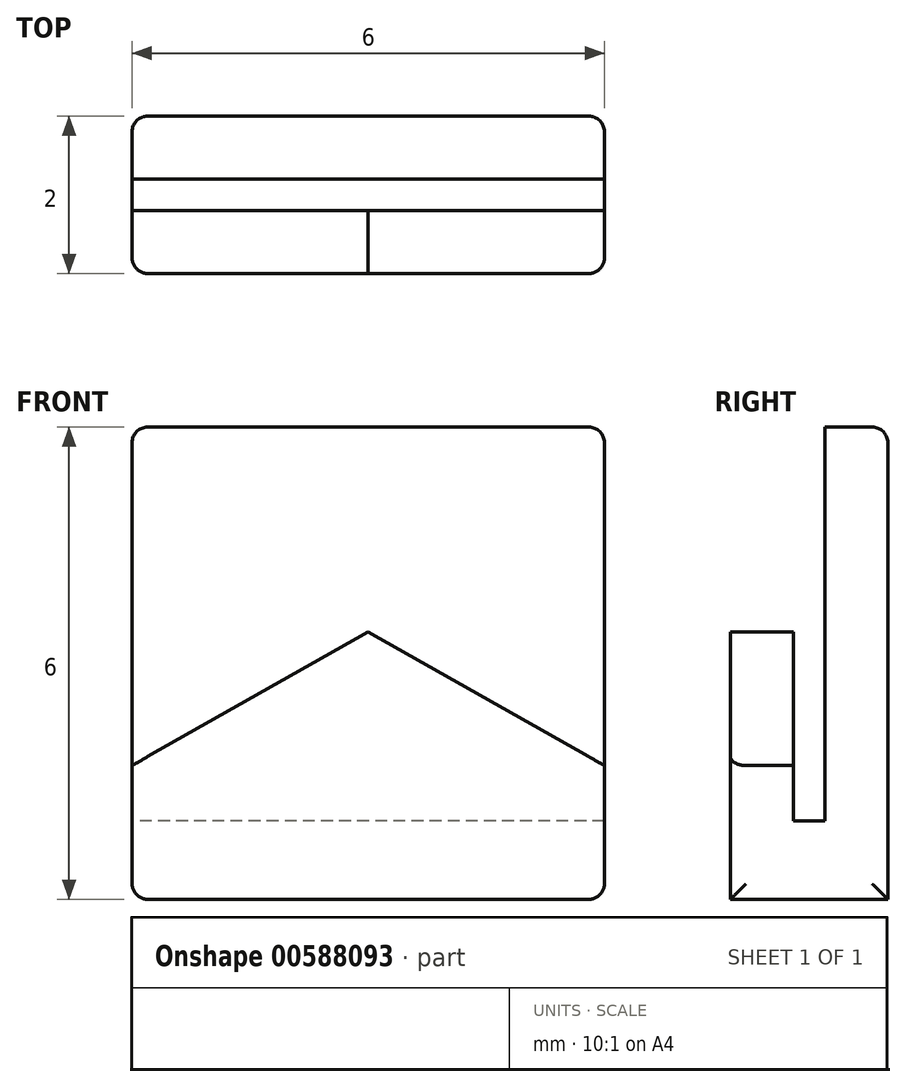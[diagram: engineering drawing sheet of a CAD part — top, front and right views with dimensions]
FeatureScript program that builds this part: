
annotation { "Feature Type Name" : "Feature", "Feature Type Description" : "" }
export const myFeature = defineFeature(function(context is Context, id is Id, definition is map)
    precondition{}
    {
        {
            var Q0;
            Q0=qCreatedBy(makeId("Top.planeOp"),FACE);
            var sketch = newSketch(context, id + "F0", { "sketchPlane" : qUnion([Q0])});
            skLineSegment(sketch, "E0.bottom", {"start": v(3, -1) * mm, "end": v(-3, -1) * mm});
            skLineSegment(sketch, "E0.top", {"start": v(3, 1) * mm, "end": v(-3, 1) * mm});
            skLineSegment(sketch, "E0.left", {"start": v(3, -1) * mm, "end": v(3, 1) * mm});
            skLineSegment(sketch, "E0.right", {"start": v(-3, -1) * mm, "end": v(-3, 1) * mm});
            skPoint(sketch, "E0.middle", {"position": v(0, 0) * mm});
            skLineSegment(sketch, "E1.bottom", {"start": v(3, 0.2) * mm, "end": v(-3, 0.2) * mm});
            skLineSegment(sketch, "E1.top", {"start": v(3, -0.2) * mm, "end": v(-3, -0.2) * mm});
            skLineSegment(sketch, "E1.left", {"start": v(3, 0.2) * mm, "end": v(3, -0.2) * mm});
            skLineSegment(sketch, "E1.right", {"start": v(-3, 0.2) * mm, "end": v(-3, -0.2) * mm});
            skSolve(sketch);
        }
        {
            var Q0;
            {var subQ0=sQuery(id+"F0.wireOp",EDGE,"E0.bottom");Q0=makeQuery(id+"F0.imprint","IMPRINT",FACE,{"disambiguationData":[TD([[makeQuery(id+"F0.imprint","IMPRINT",EDGE,{"derivedFrom":subQ0}),-1.0]])]});}
            var Q1;
            Q1=makeQuery(id+"F0.imprint","IMPRINT",FACE,{"disambiguationData":[TD([[makeQuery(id+"F0.imprint","IMPRINT",EDGE,{"derivedFrom":sQuery(id+"F0.wireOp",EDGE,"E1.bottom")}),1.0]])]});
            var Q2;
            {var subQ0=sQuery(id+"F0.wireOp",EDGE,"E0.top");Q2=makeQuery(id+"F0.imprint","IMPRINT",FACE,{"disambiguationData":[TD([[makeQuery(id+"F0.imprint","IMPRINT",EDGE,{"derivedFrom":subQ0}),1.0]])]});}
            extrude(context, id + "F1", {"entities" : qUnion([Q0, Q1, Q2]), "oppositeDirection" : true, "depth" : 1 * mm, "offsetDistance" : 25 * mm});
        }
        {
            var Q0;
            {var subQ0=sQuery(id+"F0.wireOp",EDGE,"E0.top");Q0=makeQuery(id+"F0.imprint","IMPRINT",FACE,{"disambiguationData":[TD([[makeQuery(id+"F0.imprint","IMPRINT",EDGE,{"derivedFrom":subQ0}),1.0]])]});}
            extrude(context, id + "F2", {"entities" : qUnion([Q0]), "operationType" : NewBodyOperationType.ADD, "depth" : 5 * mm, "offsetDistance" : 25 * mm});
        }
        {
            var Q0;
            {var subQ0=sQuery(id+"F0.wireOp",EDGE,"E0.bottom");Q0=makeQuery(id+"F0.imprint","IMPRINT",FACE,{"disambiguationData":[TD([[makeQuery(id+"F0.imprint","IMPRINT",EDGE,{"derivedFrom":subQ0}),-1.0]])]});}
            extrude(context, id + "F3", {"entities" : qUnion([Q0]), "operationType" : NewBodyOperationType.ADD, "depth" : 2.4 * mm, "offsetDistance" : 25 * mm});
        }
        {
            var Q0;
            {var subQ0=sQuery(id+"F0.wireOp",EDGE,"E0.bottom");Q0=makeQuery(id+"F3.boolean.opBoolean","MERGE",FACE,{"derivedFrom":[makeQuery(id+"F1.opExtrude","SWEPT_FACE",FACE,{"disambiguationData":[OSD([subQ0])]}),makeQuery(id+"F3.opExtrude","SWEPT_FACE",FACE,{"disambiguationData":[OSD([subQ0])]})]});}
            var sketch = newSketch(context, id + "F4", { "sketchPlane" : qUnion([Q0])});
            skLineSegment(sketch, "E2", {"start": v(-3, 0.7) * mm, "end": v(0, 2.4) * mm});
            skLineSegment(sketch, "E3", {"start": v(0, 2.4) * mm, "end": v(3, 0.7) * mm});
            skSolve(sketch);
        }
        {
            var Q0;
            {var subQ0=sQuery(id+"F4.wireOp",EDGE,"E2");Q0=makeQuery(id+"F4.imprint","IMPRINT",FACE,{"disambiguationData":[TD([[makeQuery(id+"F4.imprint","IMPRINT",EDGE,{"derivedFrom":subQ0}),1.0]])]});}
            var Q1;
            {var subQ0=sQuery(id+"F4.wireOp",EDGE,"E3");Q1=makeQuery(id+"F4.imprint","IMPRINT",FACE,{"disambiguationData":[TD([[makeQuery(id+"F4.imprint","IMPRINT",EDGE,{"derivedFrom":subQ0}),1.0]])]});}
            extrude(context, id + "F5", {"entities" : qUnion([Q0, Q1]), "operationType" : NewBodyOperationType.REMOVE, "oppositeDirection" : true, "depth" : 1 * mm, "offsetDistance" : 25 * mm});
        }
        {
            var Q0;
            Q0=makeQuery(id+"F2.opExtrude","CAP_EDGE",EDGE,{"disambiguationData":[OSD([sQuery(id+"F0.wireOp",EDGE,"E0.left")])],"isStart":false});
            var Q1;
            Q1=makeQuery(id+"F2.opExtrude","CAP_EDGE",EDGE,{"disambiguationData":[OSD([sQuery(id+"F0.wireOp",EDGE,"E0.right")])],"isStart":false});
            var Q2;
            Q2=makeQuery(id+"F1.opExtrude","CAP_EDGE",EDGE,{"disambiguationData":[OSD([sQuery(id+"F0.wireOp",EDGE,"E0.left"),sQuery(id+"F0.wireOp",EDGE,"E1.left")])],"isStart":false});
            var Q3;
            Q3=makeQuery(id+"F1.opExtrude","CAP_EDGE",EDGE,{"disambiguationData":[OSD([sQuery(id+"F0.wireOp",EDGE,"E0.right"),sQuery(id+"F0.wireOp",EDGE,"E1.right")])],"isStart":false});
            var Q4;
            {var subQ0=sQuery(id+"F0.wireOp",EDGE,"E0.left");var subQ1=sQuery(id+"F0.wireOp",EDGE,"E0.top");Q4=makeQuery(id+"F2.boolean.opBoolean","MERGE",EDGE,{"derivedFrom":[makeQuery(id+"F1.opExtrude","SWEPT_EDGE",EDGE,{"disambiguationData":[OSD([subQ1,subQ0])]}),makeQuery(id+"F2.opExtrude","SWEPT_EDGE",EDGE,{"disambiguationData":[OSD([subQ1,subQ0])]})]});}
            var Q5;
            {var subQ0=sQuery(id+"F0.wireOp",EDGE,"E0.right");var subQ1=sQuery(id+"F0.wireOp",EDGE,"E0.top");Q5=makeQuery(id+"F2.boolean.opBoolean","MERGE",EDGE,{"derivedFrom":[makeQuery(id+"F1.opExtrude","SWEPT_EDGE",EDGE,{"disambiguationData":[OSD([subQ1,subQ0])]}),makeQuery(id+"F2.opExtrude","SWEPT_EDGE",EDGE,{"disambiguationData":[OSD([subQ1,subQ0])]})]});}
            var Q6;
            {var subQ0=sQuery(id+"F0.wireOp",EDGE,"E0.left");var subQ1=sQuery(id+"F0.wireOp",EDGE,"E0.bottom");Q6=makeQuery(id+"F3.boolean.opBoolean","MERGE",EDGE,{"derivedFrom":[makeQuery(id+"F1.opExtrude","SWEPT_EDGE",EDGE,{"disambiguationData":[OSD([subQ1,subQ0])]}),makeQuery(id+"F3.opExtrude","SWEPT_EDGE",EDGE,{"disambiguationData":[OSD([subQ1,subQ0])]})]});}
            var Q7;
            {var subQ0=sQuery(id+"F0.wireOp",EDGE,"E0.right");var subQ1=sQuery(id+"F0.wireOp",EDGE,"E0.bottom");Q7=makeQuery(id+"F3.boolean.opBoolean","MERGE",EDGE,{"derivedFrom":[makeQuery(id+"F1.opExtrude","SWEPT_EDGE",EDGE,{"disambiguationData":[OSD([subQ1,subQ0])]}),makeQuery(id+"F3.opExtrude","SWEPT_EDGE",EDGE,{"disambiguationData":[OSD([subQ1,subQ0])]})]});}
            var Q8;
            Q8=makeQuery(id+"F5.boolean.opBoolean","COPY",EDGE,{"derivedFrom":makeQuery(id+"F5.opExtrude","CAP_EDGE",EDGE,{"disambiguationData":[OSD([sQuery(id+"F4.wireOp",EDGE,"E2")])],"isStart":true})});
            var Q9;
            Q9=makeQuery(id+"F5.boolean.opBoolean","COPY",EDGE,{"derivedFrom":makeQuery(id+"F5.opExtrude","CAP_EDGE",EDGE,{"disambiguationData":[OSD([sQuery(id+"F4.wireOp",EDGE,"E3")])],"isStart":true})});
            var Q10;
            Q10=makeQuery(id+"F2.opExtrude","CAP_EDGE",EDGE,{"disambiguationData":[OSD([sQuery(id+"F0.wireOp",EDGE,"E0.top")])],"isStart":false});
            fillet(context, id + "F6", {"entities" : qUnion([Q0, Q1, Q2, Q3, Q4, Q5, Q6, Q7, Q8, Q9, Q10]), "radius" : 0.2 * mm, "tangentPropagation" : true, "allowEdgeOverflow" : false});
        }
    });
